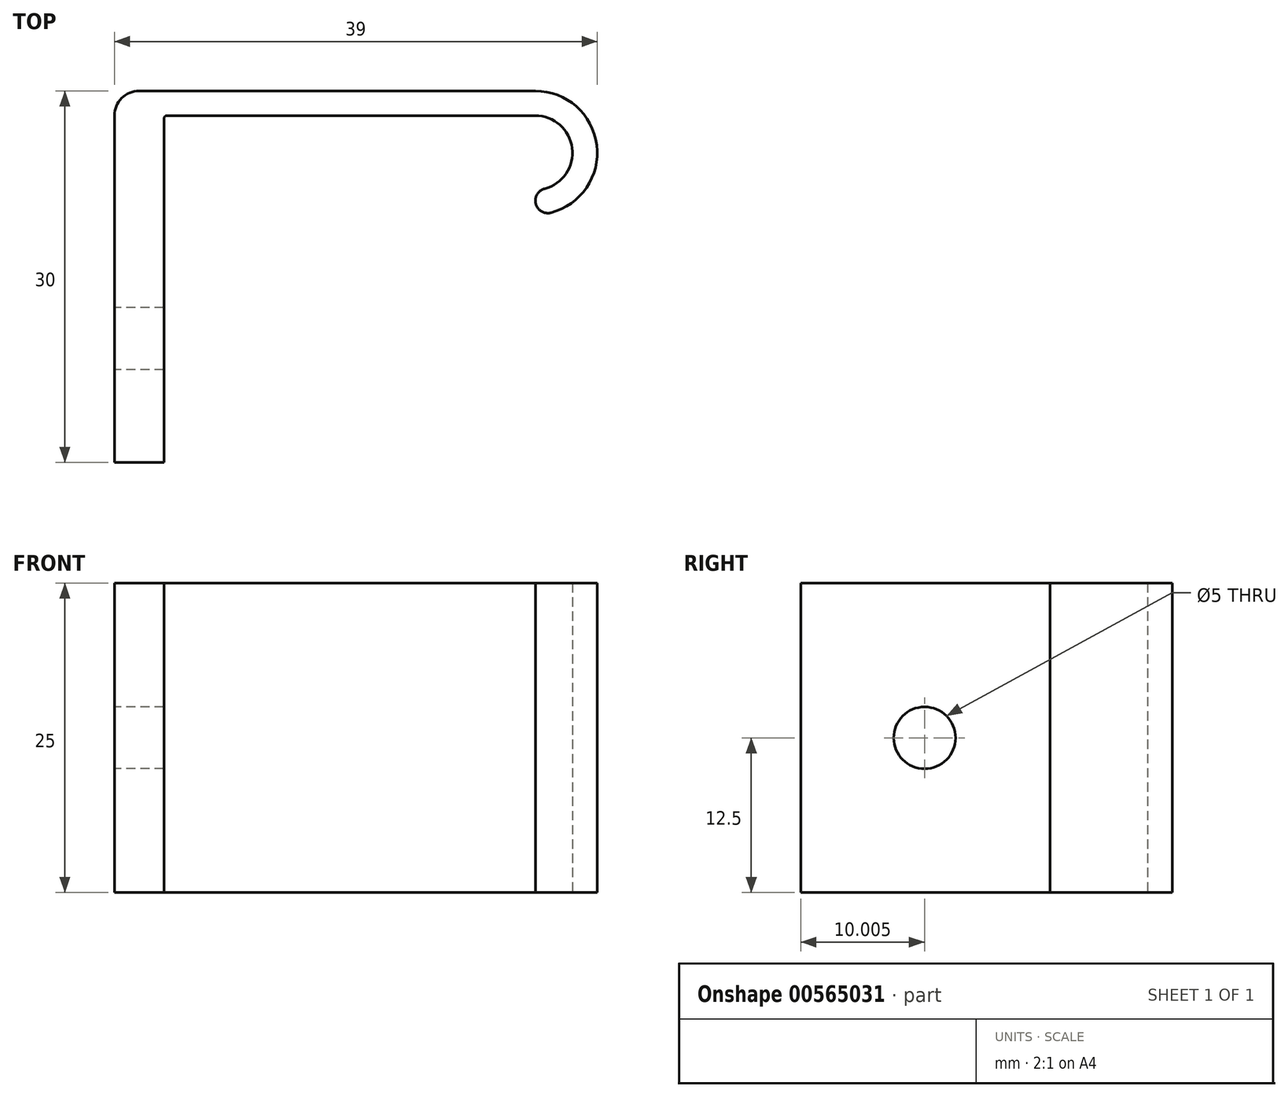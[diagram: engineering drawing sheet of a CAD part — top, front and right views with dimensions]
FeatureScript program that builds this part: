
annotation { "Feature Type Name" : "Feature", "Feature Type Description" : "" }
export const myFeature = defineFeature(function(context is Context, id is Id, definition is map)
    precondition{}
    {
        {
            var Q0;
            Q0=qCreatedBy(makeId("Top.planeOp"),FACE);
            var sketch = newSketch(context, id + "F0", { "sketchPlane" : qUnion([Q0])});
            skLineSegment(sketch, "E0.bottom", {"start": v(-11.7, 7.27) * mm, "end": v(-9.7, 7.27) * mm});
            skLineSegment(sketch, "E0.top", {"start": v(-13.7, -22.73) * mm, "end": v(-9.7, -22.73) * mm});
            skLineSegment(sketch, "E0.left", {"start": v(-13.7, 5.27) * mm, "end": v(-13.7, -22.73) * mm});
            skLineSegment(sketch, "E0.right", {"start": v(-9.7, 5.02) * mm, "end": v(-9.7, -22.73) * mm});
            skLineSegment(sketch, "E1.bottom", {"start": v(-9.7, 7.27) * mm, "end": v(20.3, 7.27) * mm});
            skLineSegment(sketch, "E1.top", {"start": v(-9.45, 5.27) * mm, "end": v(20.3, 5.27) * mm});
            skArc(sketch, "E2", {"start": v(21.55, -2.57) * mm, "mid": v(25.26, 2.9) * mm, "end": v(20.3, 7.27) * mm});
            skPoint(sketch, "E3.visualSharp", {"position": v(-13.7, 7.27) * mm});
            skArc(sketch, "E3.filletArc", {"start": v(-11.7, 7.27) * mm, "mid": v(-13.11, 6.69) * mm, "end": v(-13.7, 5.27) * mm});
            skPoint(sketch, "E4.visualSharp", {"position": v(16.3, 5.27) * mm});
            skPoint(sketch, "E5.visualSharp", {"position": v(-9.7, 5.27) * mm});
            skArc(sketch, "E5.filletArc", {"start": v(-9.45, 5.27) * mm, "mid": v(-9.62, 5.2) * mm, "end": v(-9.7, 5.02) * mm});
            skArc(sketch, "E6", {"start": v(21.05, -0.63) * mm, "mid": v(23.28, 2.65) * mm, "end": v(20.3, 5.27) * mm});
            skLineSegment(sketch, "E7", {"start": v(20.3, -1.6) * mm, "end": v(20.3, -1.6) * mm});
            skPoint(sketch, "E8.visualSharp", {"position": v(20.3, -2.73) * mm});
            skArc(sketch, "E8.filletArc", {"start": v(20.3, -1.6) * mm, "mid": v(20.7, -2.39) * mm, "end": v(21.55, -2.57) * mm});
            skPoint(sketch, "E9.visualSharp", {"position": v(20.3, -0.73) * mm});
            skArc(sketch, "E9.filletArc", {"start": v(21.05, -0.63) * mm, "mid": v(20.51, -0.99) * mm, "end": v(20.3, -1.6) * mm});
            skSolve(sketch);
        }
        {
            var Q0;
            Q0=makeQuery(id+"F0.imprint","IMPRINT",FACE,{"disambiguationData":[TD([[makeQuery(id+"F0.imprint","IMPRINT",EDGE,{"derivedFrom":sQuery(id+"F0.wireOp",EDGE,"E0.bottom")}),-1.0]])]});
            extrude(context, id + "F1", {"entities" : qUnion([Q0]), "depth" : 25 * mm, "offsetDistance" : 25 * mm});
        }
        {
            var Q0;
            Q0=makeQuery(id+"F1.opExtrude","SWEPT_FACE",FACE,{"disambiguationData":[OSD([sQuery(id+"F0.wireOp",EDGE,"E0.left")])]});
            var sketch = newSketch(context, id + "F2", { "sketchPlane" : qUnion([Q0])});
            skCircle(sketch, "E10", {"center": v(12.73, 12.5) * mm, "radius": 2.5 * mm});
            skSolve(sketch);
        }
        {
            var Q0;
            Q0=makeQuery(id+"F2.imprint","IMPRINT",FACE,{"disambiguationData":[TD([[makeQuery(id+"F2.imprint","IMPRINT",EDGE,{"derivedFrom":sQuery(id+"F2.wireOp",EDGE,"E10")}),1.0]])]});
            extrude(context, id + "F3", {"entities" : qUnion([Q0]), "operationType" : NewBodyOperationType.REMOVE, "endBound" : BoundingType.UP_TO_NEXT, "oppositeDirection" : true, "depth" : 8 * mm, "offsetDistance" : 25 * mm});
        }
    });
